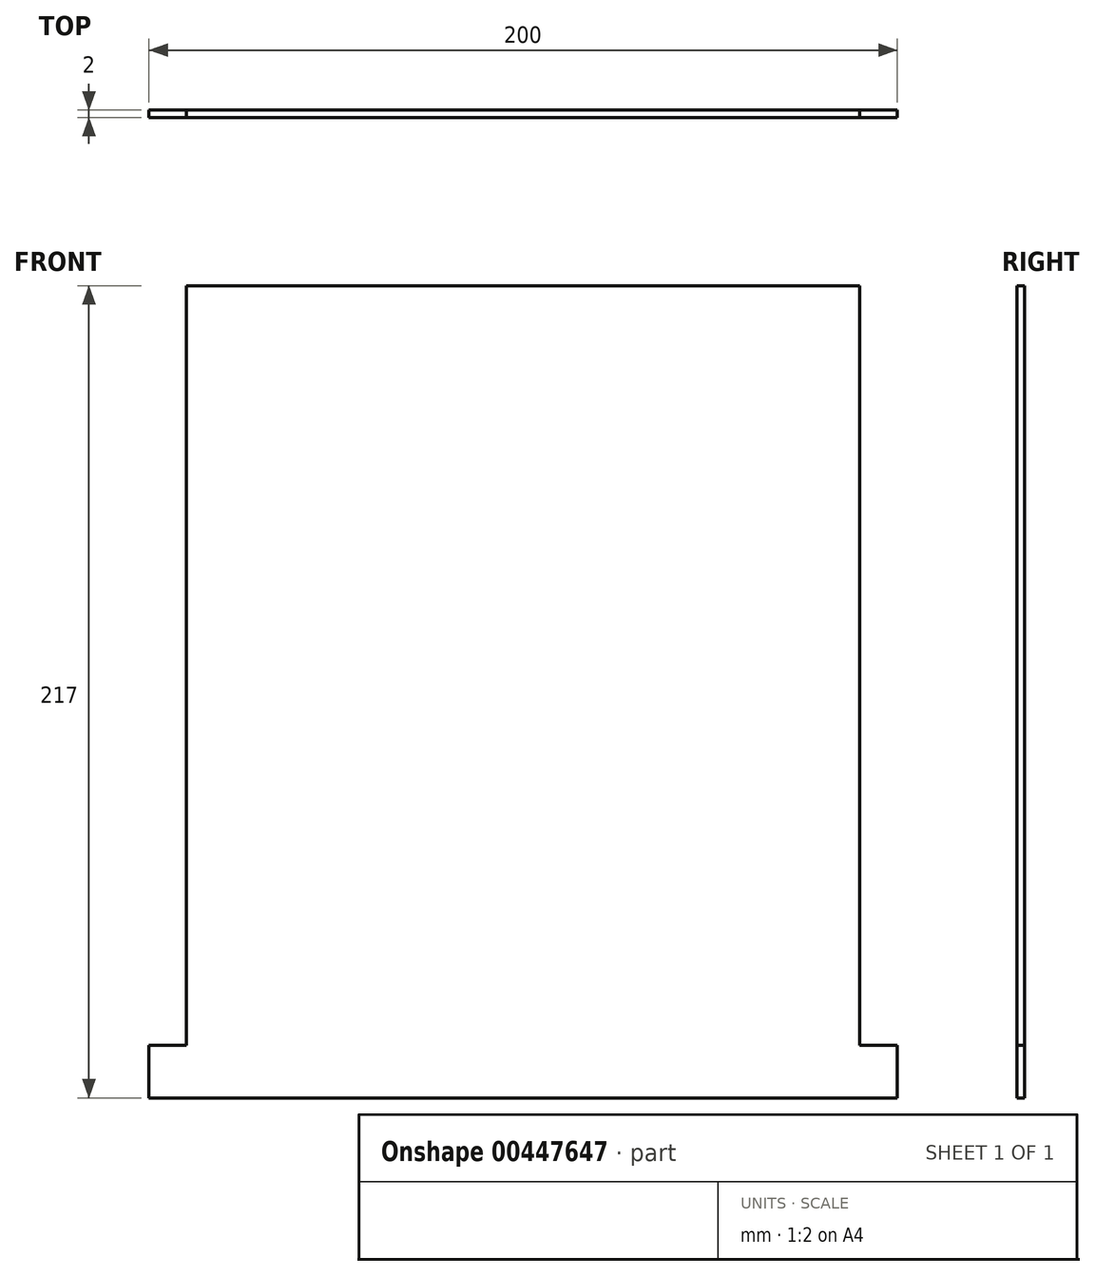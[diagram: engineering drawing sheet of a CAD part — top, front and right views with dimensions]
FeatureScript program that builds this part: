
annotation { "Feature Type Name" : "Feature", "Feature Type Description" : "" }
export const myFeature = defineFeature(function(context is Context, id is Id, definition is map)
    precondition{}
    {
        {
            var Q0;
            Q0=qCreatedBy(makeId("Front.planeOp"),FACE);
            var sketch = newSketch(context, id + "F0", { "sketchPlane" : qUnion([Q0])});
            skLineSegment(sketch, "E0.bottom", {"start": v(90, -101.5) * mm, "end": v(-90, -101.5) * mm});
            skLineSegment(sketch, "E0.top", {"start": v(90, 101.5) * mm, "end": v(-90, 101.5) * mm});
            skLineSegment(sketch, "E0.left", {"start": v(90, -101.5) * mm, "end": v(90, 101.5) * mm});
            skLineSegment(sketch, "E0.right", {"start": v(-90, -101.5) * mm, "end": v(-90, 101.5) * mm});
            skPoint(sketch, "E0.middle", {"position": v(0, 0) * mm});
            skLineSegment(sketch, "E1.bottom", {"start": v(100, -115.5) * mm, "end": v(-100, -115.5) * mm});
            skLineSegment(sketch, "E1.top", {"start": v(100, -101.5) * mm, "end": v(-100, -101.5) * mm});
            skLineSegment(sketch, "E1.left", {"start": v(100, -115.5) * mm, "end": v(100, -101.5) * mm});
            skLineSegment(sketch, "E1.right", {"start": v(-100, -115.5) * mm, "end": v(-100, -101.5) * mm});
            skPoint(sketch, "E1.middle", {"position": v(0, -108.5) * mm});
            skPoint(sketch, "E2", {"position": v(0, -101.5) * mm});
            skSolve(sketch);
        }
        {
            var Q0;
            Q0 = qSketchRegion(id + "F0", true);
            extrude(context, id + "F1", {"entities" : qUnion([Q0]), "depth" : 2 * mm});
        }
    });
